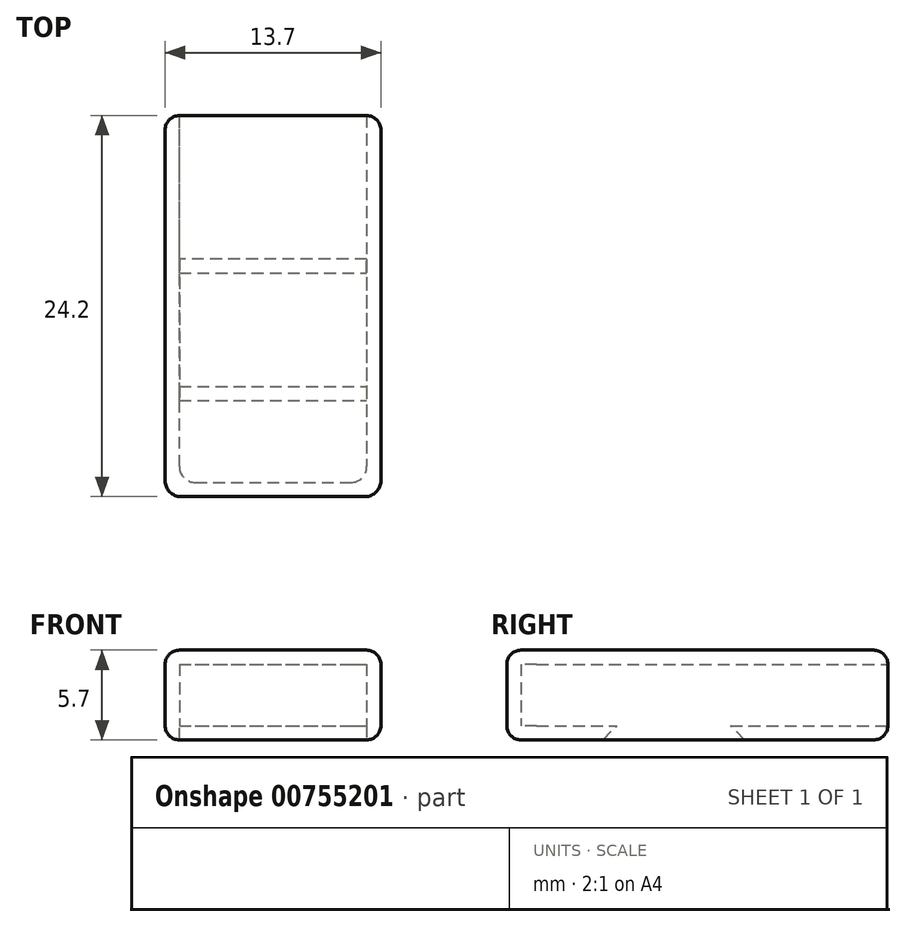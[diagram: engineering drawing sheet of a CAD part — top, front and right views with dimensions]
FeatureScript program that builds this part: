
annotation { "Feature Type Name" : "Feature", "Feature Type Description" : "" }
export const myFeature = defineFeature(function(context is Context, id is Id, definition is map)
    precondition{}
    {
        {
            var Q0;
            Q0=qCreatedBy(makeId("Top.planeOp"),FACE);
            var sketch = newSketch(context, id + "F0", { "sketchPlane" : qUnion([Q0])});
            skLineSegment(sketch, "E0.top", {"start": v(-5.95, -11.2) * mm, "end": v(5.95, -11.2) * mm});
            skLineSegment(sketch, "E0.left", {"start": v(-5.95, 11.2) * mm, "end": v(-5.95, -11.2) * mm});
            skLineSegment(sketch, "E0.right", {"start": v(5.95, 11.2) * mm, "end": v(5.95, -11.2) * mm});
            skPoint(sketch, "E0.middle", {"position": v(0, 0) * mm});
            skLineSegment(sketch, "E1.bottom", {"start": v(-6.85, 12.1) * mm, "end": v(6.85, 12.1) * mm});
            skLineSegment(sketch, "E1.top", {"start": v(-6.85, -12.1) * mm, "end": v(6.85, -12.1) * mm});
            skLineSegment(sketch, "E1.left", {"start": v(-6.85, 12.1) * mm, "end": v(-6.85, -12.1) * mm});
            skLineSegment(sketch, "E1.right", {"start": v(6.85, 12.1) * mm, "end": v(6.85, -12.1) * mm});
            skLineSegment(sketch, "E2", {"start": v(-5.95, 11.2) * mm, "end": v(-5.95, 12.1) * mm});
            skLineSegment(sketch, "E3", {"start": v(5.95, 11.2) * mm, "end": v(5.95, 12.1) * mm});
            skSolve(sketch);
        }
        {
            var Q0;
            Q0=makeQuery(id+"F0.imprint","IMPRINT",FACE,{"disambiguationData":[TD([[makeQuery(id+"F0.imprint","IMPRINT",EDGE,{"derivedFrom":sQuery(id+"F0.wireOp",EDGE,"E0.top")}),1.0]])]});
            var Q1;
            Q1=makeQuery(id+"F0.imprint","IMPRINT",FACE,{"disambiguationData":[TD([[makeQuery(id+"F0.imprint","IMPRINT",EDGE,{"derivedFrom":sQuery(id+"F0.wireOp",EDGE,"E0.top")}),-1.0]])]});
            extrude(context, id + "F1", {"entities" : qUnion([Q0, Q1]), "depth" : (1.75 + 0.2 + 0.9) * mm, "offsetDistance" : 25 * mm});
        }
        {
            var Q0;
            Q0=makeQuery(id+"F0.imprint","IMPRINT",FACE,{"disambiguationData":[TD([[makeQuery(id+"F0.imprint","IMPRINT",EDGE,{"derivedFrom":sQuery(id+"F0.wireOp",EDGE,"E0.top")}),1.0]])]});
            extrude(context, id + "F2", {"entities" : qUnion([Q0]), "operationType" : NewBodyOperationType.REMOVE, "depth" : (1.75 + 0.2) * mm, "offsetDistance" : 25 * mm});
        }
        {
            var Q0;
            Q0=makeQuery(id+"F0.imprint","IMPRINT",FACE,{"disambiguationData":[TD([[makeQuery(id+"F0.imprint","IMPRINT",EDGE,{"derivedFrom":sQuery(id+"F0.wireOp",EDGE,"E0.top")}),1.0]])]});
            var Q1;
            Q1=makeQuery(id+"F0.imprint","IMPRINT",FACE,{"disambiguationData":[TD([[makeQuery(id+"F0.imprint","IMPRINT",EDGE,{"derivedFrom":sQuery(id+"F0.wireOp",EDGE,"E0.top")}),-1.0]])]});
            extrude(context, id + "F3", {"entities" : qUnion([Q0, Q1]), "operationType" : NewBodyOperationType.ADD, "oppositeDirection" : true, "depth" : (1.75 + 0.2 + 0.9) * mm, "offsetDistance" : 25 * mm});
        }
        {
            var Q0;
            Q0=makeQuery(id+"F0.imprint","IMPRINT",FACE,{"disambiguationData":[TD([[makeQuery(id+"F0.imprint","IMPRINT",EDGE,{"derivedFrom":sQuery(id+"F0.wireOp",EDGE,"E0.top")}),1.0]])]});
            extrude(context, id + "F4", {"entities" : qUnion([Q0]), "operationType" : NewBodyOperationType.REMOVE, "oppositeDirection" : true, "depth" : (1.75 + 0.2) * mm, "offsetDistance" : 25 * mm});
        }
        {
            var Q0;
            {var subQ0=sQuery(id+"F0.wireOp",EDGE,"E0.right");var subQ1=sQuery(id+"F0.wireOp",EDGE,"E0.top");Q0=makeQuery(id+"F4.boolean.opBoolean","MERGE",EDGE,{"derivedFrom":[makeQuery(id+"F2.boolean.opBoolean","COPY",EDGE,{"derivedFrom":makeQuery(id+"F2.opExtrude","SWEPT_EDGE",EDGE,{"disambiguationData":[OSD([subQ1,subQ0])]})}),makeQuery(id+"F4.opExtrude","SWEPT_EDGE",EDGE,{"disambiguationData":[OSD([subQ1,subQ0])]})]});}
            var Q1;
            {var subQ0=sQuery(id+"F0.wireOp",EDGE,"E0.left");var subQ1=sQuery(id+"F0.wireOp",EDGE,"E0.top");Q1=makeQuery(id+"F4.boolean.opBoolean","MERGE",EDGE,{"derivedFrom":[makeQuery(id+"F2.boolean.opBoolean","COPY",EDGE,{"derivedFrom":makeQuery(id+"F2.opExtrude","SWEPT_EDGE",EDGE,{"disambiguationData":[OSD([subQ1,subQ0])]})}),makeQuery(id+"F4.opExtrude","SWEPT_EDGE",EDGE,{"disambiguationData":[OSD([subQ1,subQ0])]})]});}
            var Q2;
            {var subQ0=sQuery(id+"F0.wireOp",EDGE,"E1.left");var subQ1=sQuery(id+"F0.wireOp",EDGE,"E1.top");Q2=makeQuery(id+"F3.boolean.opBoolean","MERGE",EDGE,{"derivedFrom":[makeQuery(id+"F1.opExtrude","SWEPT_EDGE",EDGE,{"disambiguationData":[OSD([subQ1,subQ0])]}),makeQuery(id+"F3.opExtrude","SWEPT_EDGE",EDGE,{"disambiguationData":[OSD([subQ1,subQ0])]})]});}
            var Q3;
            {var subQ0=sQuery(id+"F0.wireOp",EDGE,"E1.right");var subQ1=sQuery(id+"F0.wireOp",EDGE,"E1.top");Q3=makeQuery(id+"F3.boolean.opBoolean","MERGE",EDGE,{"derivedFrom":[makeQuery(id+"F1.opExtrude","SWEPT_EDGE",EDGE,{"disambiguationData":[OSD([subQ1,subQ0])]}),makeQuery(id+"F3.opExtrude","SWEPT_EDGE",EDGE,{"disambiguationData":[OSD([subQ1,subQ0])]})]});}
            fillet(context, id + "F5", {"entities" : qUnion([Q0, Q1, Q2, Q3]), "radius" : 1 * mm, "tangentPropagation" : true, "allowEdgeOverflow" : false});
        }
        {
            var Q0;
            Q0=qCreatedBy(makeId("Top.planeOp"),FACE);
            var sketch = newSketch(context, id + "F6", { "sketchPlane" : qUnion([Q0])});
            skLineSegment(sketch, "E4", {"start": v(0, 0) * mm, "end": v(0, 1) * mm});
            skLineSegment(sketch, "E5.top", {"start": v(-5.95, -4) * mm, "end": v(5.95, -4) * mm});
            skLineSegment(sketch, "E5.left", {"start": v(-5.95, 1) * mm, "end": v(-5.95, -4) * mm});
            skLineSegment(sketch, "E5.right", {"start": v(5.95, 1) * mm, "end": v(5.95, -4) * mm});
            skPoint(sketch, "E5.middle", {"position": v(0, 1) * mm});
            skLineSegment(sketch, "E6", {"start": v(0, 1) * mm, "end": v(-5.95, 1) * mm});
            skLineSegment(sketch, "E7", {"start": v(0, 1) * mm, "end": v(5.95, 1) * mm});
            skPoint(sketch, "E5.bottom.start.orphan", {"position": v(-5.95, 6) * mm});
            skPoint(sketch, "E8.orphan", {"position": v(5.95, 6) * mm});
            skSolve(sketch);
        }
        {
            var Q0;
            Q0 = qSketchRegion(id + "F6", true);
            extrude(context, id + "F7", {"entities" : qUnion([Q0]), "operationType" : NewBodyOperationType.REMOVE, "oppositeDirection" : true, "depth" : 25 * mm, "offsetDistance" : 25 * mm});
        }
        {
            var Q0;
            Q0=makeQuery(id+"F7.boolean.opBoolean","INTERSECT",EDGE,{"derivedFrom":[makeQuery(id+"F3.opExtrude","CAP_FACE",FACE,{"disambiguationData":[OSD([sQuery(id+"F0.wireOp",EDGE,"E1.bottom"),sQuery(id+"F0.wireOp",EDGE,"E1.top"),sQuery(id+"F0.wireOp",EDGE,"E1.left"),sQuery(id+"F0.wireOp",EDGE,"E1.right")])],"isStart":false}),makeQuery(id+"F7.opExtrude","SWEPT_FACE",FACE,{"disambiguationData":[OSD([sQuery(id+"F6.wireOp",EDGE,"E5.top")])]})]});
            var Q1;
            Q1=makeQuery(id+"F7.boolean.opBoolean","INTERSECT",EDGE,{"derivedFrom":[makeQuery(id+"F3.opExtrude","CAP_FACE",FACE,{"disambiguationData":[OSD([sQuery(id+"F0.wireOp",EDGE,"E1.bottom"),sQuery(id+"F0.wireOp",EDGE,"E1.top"),sQuery(id+"F0.wireOp",EDGE,"E1.left"),sQuery(id+"F0.wireOp",EDGE,"E1.right")])],"isStart":false}),makeQuery(id+"F7.opExtrude","SWEPT_FACE",FACE,{"disambiguationData":[OSD([sQuery(id+"F6.wireOp",EDGE,"E6"),sQuery(id+"F6.wireOp",EDGE,"E7")])]})]});
            chamfer(context, id + "F8", {"entities" : qUnion([Q0, Q1]), "width" : 2 * mm, "tangentPropagation" : true});
        }
        {
            var Q0;
            {var subQ0=sQuery(id+"F0.wireOp",EDGE,"E1.right");var subQ1=sQuery(id+"F0.wireOp",EDGE,"E1.bottom");Q0=makeQuery(id+"F3.boolean.opBoolean","MERGE",EDGE,{"derivedFrom":[makeQuery(id+"F1.opExtrude","SWEPT_EDGE",EDGE,{"disambiguationData":[OSD([subQ1,subQ0])]}),makeQuery(id+"F3.opExtrude","SWEPT_EDGE",EDGE,{"disambiguationData":[OSD([subQ1,subQ0])]})]});}
            var Q1;
            {var subQ0=sQuery(id+"F0.wireOp",EDGE,"E1.left");var subQ1=sQuery(id+"F0.wireOp",EDGE,"E1.bottom");Q1=makeQuery(id+"F3.boolean.opBoolean","MERGE",EDGE,{"derivedFrom":[makeQuery(id+"F1.opExtrude","SWEPT_EDGE",EDGE,{"disambiguationData":[OSD([subQ1,subQ0])]}),makeQuery(id+"F3.opExtrude","SWEPT_EDGE",EDGE,{"disambiguationData":[OSD([subQ1,subQ0])]})]});}
            var Q2;
            Q2=makeQuery(id+"F3.opExtrude","CAP_EDGE",EDGE,{"disambiguationData":[OSD([sQuery(id+"F0.wireOp",EDGE,"E1.bottom")])],"isStart":false});
            var Q3;
            Q3=makeQuery(id+"F1.opExtrude","CAP_EDGE",EDGE,{"disambiguationData":[OSD([sQuery(id+"F0.wireOp",EDGE,"E1.bottom")])],"isStart":false});
            var Q4;
            Q4=makeQuery(id+"F3.opExtrude","CAP_EDGE",EDGE,{"disambiguationData":[OSD([sQuery(id+"F0.wireOp",EDGE,"E1.right")])],"isStart":false});
            var Q5;
            Q5=makeQuery(id+"F1.opExtrude","CAP_EDGE",EDGE,{"disambiguationData":[OSD([sQuery(id+"F0.wireOp",EDGE,"E1.top")])],"isStart":false});
            fillet(context, id + "F9", {"entities" : qUnion([Q0, Q1, Q2, Q3, Q4, Q5]), "radius" : 0.9 * mm, "tangentPropagation" : true, "allowEdgeOverflow" : false});
        }
    });
